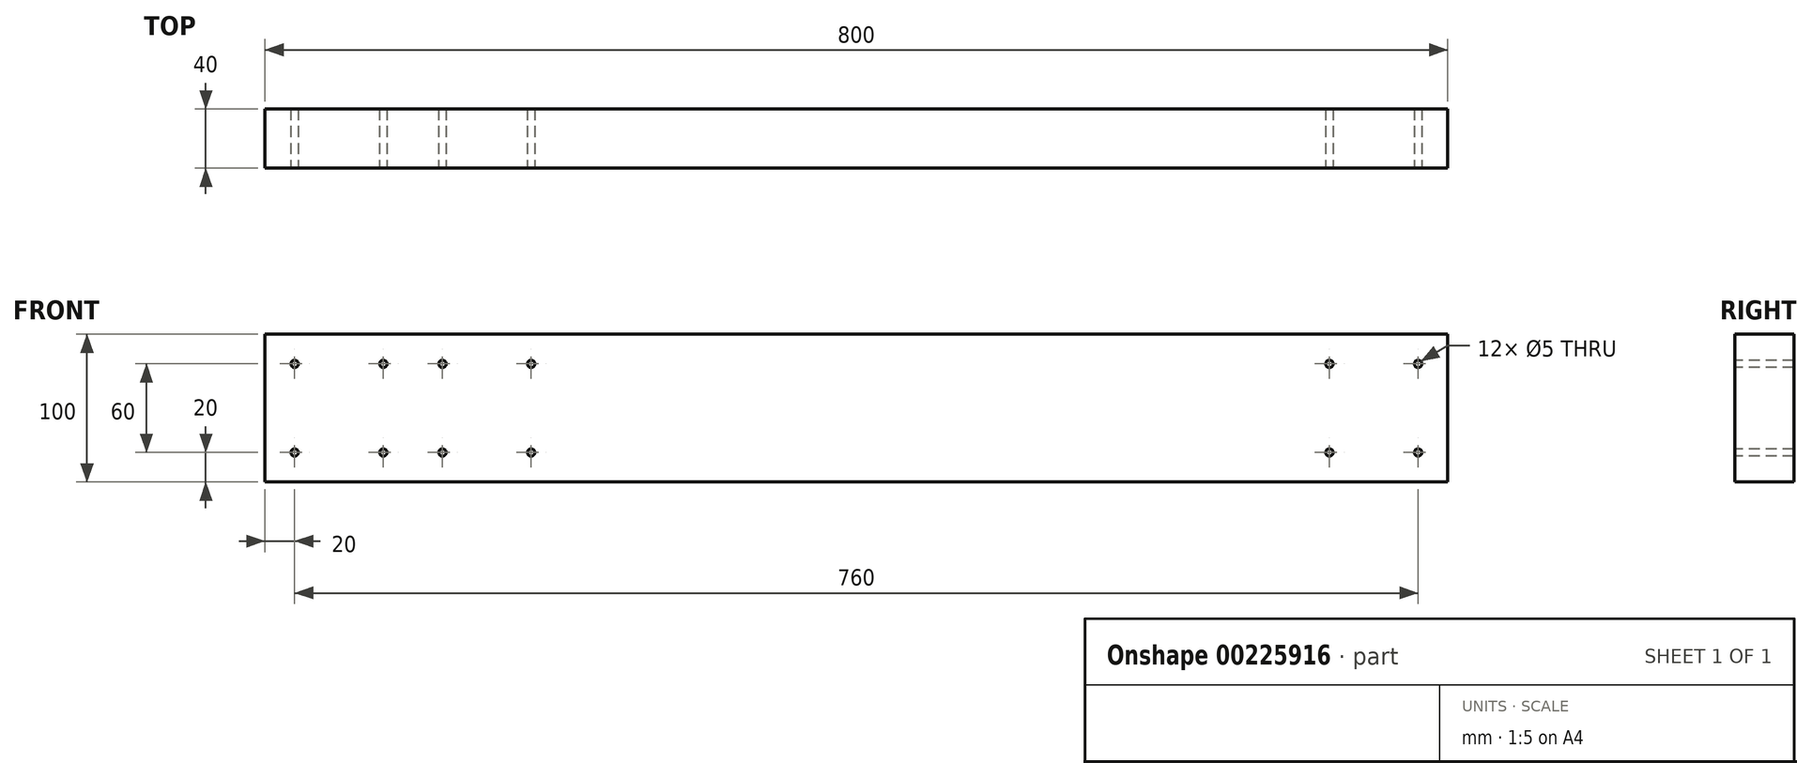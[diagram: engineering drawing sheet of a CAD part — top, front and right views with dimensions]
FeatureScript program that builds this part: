
annotation { "Feature Type Name" : "Feature", "Feature Type Description" : "" }
export const myFeature = defineFeature(function(context is Context, id is Id, definition is map)
    precondition{}
    {
        {
            var Q0;
            Q0=qCreatedBy(makeId("Front.planeOp"),FACE);
            var sketch = newSketch(context, id + "F0", { "sketchPlane" : qUnion([Q0])});
            skLineSegment(sketch, "E0.bottom", {"start": v(-400, 50) * mm, "end": v(400, 50) * mm});
            skLineSegment(sketch, "E0.top", {"start": v(-400, -50) * mm, "end": v(400, -50) * mm});
            skLineSegment(sketch, "E0.left", {"start": v(-400, 50) * mm, "end": v(-400, -50) * mm});
            skLineSegment(sketch, "E0.right", {"start": v(400, 50) * mm, "end": v(400, -50) * mm});
            skLineSegment(sketch, "E1", {"start": v(0, 50) * mm, "end": v(0, -50) * mm, "construction": true});
            skLineSegment(sketch, "E2", {"start": v(-400, 0) * mm, "end": v(400, 0) * mm, "construction": true});
            skSolve(sketch);
        }
        {
            var Q0;
            Q0=makeQuery(id+"F0.imprint","IMPRINT",FACE,{"disambiguationData":[TD([[makeQuery(id+"F0.imprint","IMPRINT",EDGE,{"derivedFrom":sQuery(id+"F0.wireOp",EDGE,"E0.bottom")}),-1.0]])]});
            extrude(context, id + "F1", {"entities" : qUnion([Q0]), "endBound" : BoundingType.SYMMETRIC, "depth" : 40 * mm});
        }
        {
            var Q0;
            Q0=makeQuery(id+"F1.opExtrude","CAP_FACE",FACE,{"disambiguationData":[OSD([sQuery(id+"F0.wireOp",EDGE,"E0.bottom"),sQuery(id+"F0.wireOp",EDGE,"E0.top"),sQuery(id+"F0.wireOp",EDGE,"E0.left"),sQuery(id+"F0.wireOp",EDGE,"E0.right")])],"isStart":false});
            var sketch = newSketch(context, id + "F2", { "sketchPlane" : qUnion([Q0])});
            skPoint(sketch, "E3", {"position": v(-380, 30) * mm});
            skPoint(sketch, "E4", {"position": v(-320, 30) * mm});
            skPoint(sketch, "E5", {"position": v(-380, -30) * mm});
            skPoint(sketch, "E6", {"position": v(-320, -30) * mm});
            skPoint(sketch, "E7", {"position": v(-280, 30) * mm});
            skPoint(sketch, "E8", {"position": v(-220, 30) * mm});
            skPoint(sketch, "E9", {"position": v(-280, -30) * mm});
            skPoint(sketch, "E10", {"position": v(-220, -30) * mm});
            skPoint(sketch, "E11", {"position": v(380, 30) * mm});
            skPoint(sketch, "E12", {"position": v(320, 30) * mm});
            skPoint(sketch, "E13", {"position": v(320, -30) * mm});
            skPoint(sketch, "E14", {"position": v(380, -30) * mm});
            skSolve(sketch);
        }
        {
            var Q0;
            Q0=sQuery(id+"F2.wireOp",VERTEX,"E3");
            var Q1;
            Q1=sQuery(id+"F2.wireOp",VERTEX,"E5");
            var Q2;
            Q2=sQuery(id+"F2.wireOp",VERTEX,"E4");
            var Q3;
            Q3=sQuery(id+"F2.wireOp",VERTEX,"E6");
            var Q4;
            Q4=sQuery(id+"F2.wireOp",VERTEX,"E7");
            var Q5;
            Q5=sQuery(id+"F2.wireOp",VERTEX,"E9");
            var Q6;
            Q6=sQuery(id+"F2.wireOp",VERTEX,"E10");
            var Q7;
            Q7=sQuery(id+"F2.wireOp",VERTEX,"E8");
            var Q8;
            Q8=sQuery(id+"F2.wireOp",VERTEX,"E11");
            var Q9;
            Q9=sQuery(id+"F2.wireOp",VERTEX,"E12");
            var Q10;
            Q10=sQuery(id+"F2.wireOp",VERTEX,"E13");
            var Q11;
            Q11=sQuery(id+"F2.wireOp",VERTEX,"E14");
            var Q12;
            Q12=makeQuery(id+"F1.opExtrude","SWEPT_BODY",BODY,{"disambiguationData":[OSD([sQuery(id+"F0.wireOp",EDGE,"E0.bottom"),sQuery(id+"F0.wireOp",EDGE,"E0.top"),sQuery(id+"F0.wireOp",EDGE,"E0.left"),sQuery(id+"F0.wireOp",EDGE,"E0.right")])]});
            hole(context, id + "F3", {"style" : HoleStyle.SIMPLE, "endStyle" : HoleEndStyle.THROUGH, "holeDiameter" : 5 * mm, "locations" : qUnion([Q0, Q1, Q2, Q3, Q4, Q5, Q6, Q7, Q8, Q9, Q10, Q11]), "scope" : qUnion([Q12]), "isTappedThrough" : true});
        }
    });
